# Revit family: S36-PDx119-xxFSW8xxLPOxxxx
name_source: partatom
category: Leuchten
revit_build: Autodesk Revit 2017 (Build: 20190508_0315(x64)
units: mm (PartAtom-declared; Revit-internal decimal feet)

## family parameters
Basisbauteil = Fläche
Beim Laden mit Abzugskörper schneiden = Nein
Bemaßung runder Anschluss = Durchmesser verwenden
Gemeinsam genutzt = Nein
Lichtquelle = Ja
OmniClass-Nummer = 23.80.70.11
OmniClass-Titel = Luminaries for Internal Lighting
Raumberechnungspunkt = Nein
Teiletyp = Normal

## types (9) — shared parameters
Baugruppenkennzeichen = D5020200
Emissionsform beim Rendern sichtbar = Nein
Farbfilter = 16777215
Farbtemperaturverschiebung bei Dämpfen der Lampe = <Keine Auswahl>
Hersteller = Spectral
Lampe = LED
Neigungswinkel = 90.00°
URL = https://www.spectral-lighting.com
Von Breite des Rechtecks ausssenden = 1189 mm  [stored 3.90092 ft]
Von Länge des Rechtecks aussenden = 36 mm  [stored 0.11811 ft]
brand = Spectral
conformity mark = CE
electrical safety class = 1
height = 72 mm  [stored 0.23622 ft]
ingress protection (IP) code = IP20
length = 1190 mm  [stored 3.9042 ft]
nominal frequency = 50-60Hz
nominal voltage = 230
voltage type (AC, DC, UC) = AC
weight = 3.1 kg
width = 36 mm  [stored 0.11811 ft]
zero-valued in all types: Vorgabe-Ansicht

## per-type parameters (varying)
| type | Datei für fotometrisches Netz | Modell | Scheinlast | rated input power |
| S36-PD119 NDFSW830LPO0250 | S36-PD149 DAFWS840LPO0300.IES | SPG0620056AQ | 22 VA | 22 |
| S36-PD119 DAFSW830LPO0250 | S36-PD149 DAFWS840LPO0300.IES | SPG0630056AQ | 22 VA | 22 |
| S36-PD119 NDFSW840LPO0250 | S36-PD149 DAFWS840LPO0300.IES | SPG0620038AQ | 22 VA | 22 |
| S36-PD119 DAFSW840LPO0250 | S36-PD149 DAFWS840LPO0300.IES | SPG0630038AQ | 22 VA | 22 |
| S36-PDI119 NDFSW830LPO0550 | S36-PDI149 DAFWS840LPO0700.IES | SPG0620062AQ | 44 VA | 44 |
| S36-PDI119 DAFSW830LPO0550 | S36-PDI149 DAFWS840LPO0700.IES | SPG0630062AQ | 44 VA | 44 |
| S36-PDI119 NDFSW840LPO0550 | S36-PDI149 DAFWS840LPO0700.IES | SPG0620032AQ | 44 VA | 44 |
| S36-PDI119 DAFSW840LPO0550 | S36-PDI149 DAFWS840LPO0700.IES | SPG0630032AQ | 44 VA | 44 |
| S36-PD119 DAFSWTWLPO0250 | S36-PD149 DAFWS840LPO0300.IES | SPG0630086AQ | 22 VA | 22 |

note: column(s) folded — value = type name in every type: product name

note: [stored X ft] marks values corroborated as IEEE doubles in the binary element streams (Revit-internal decimal feet)
